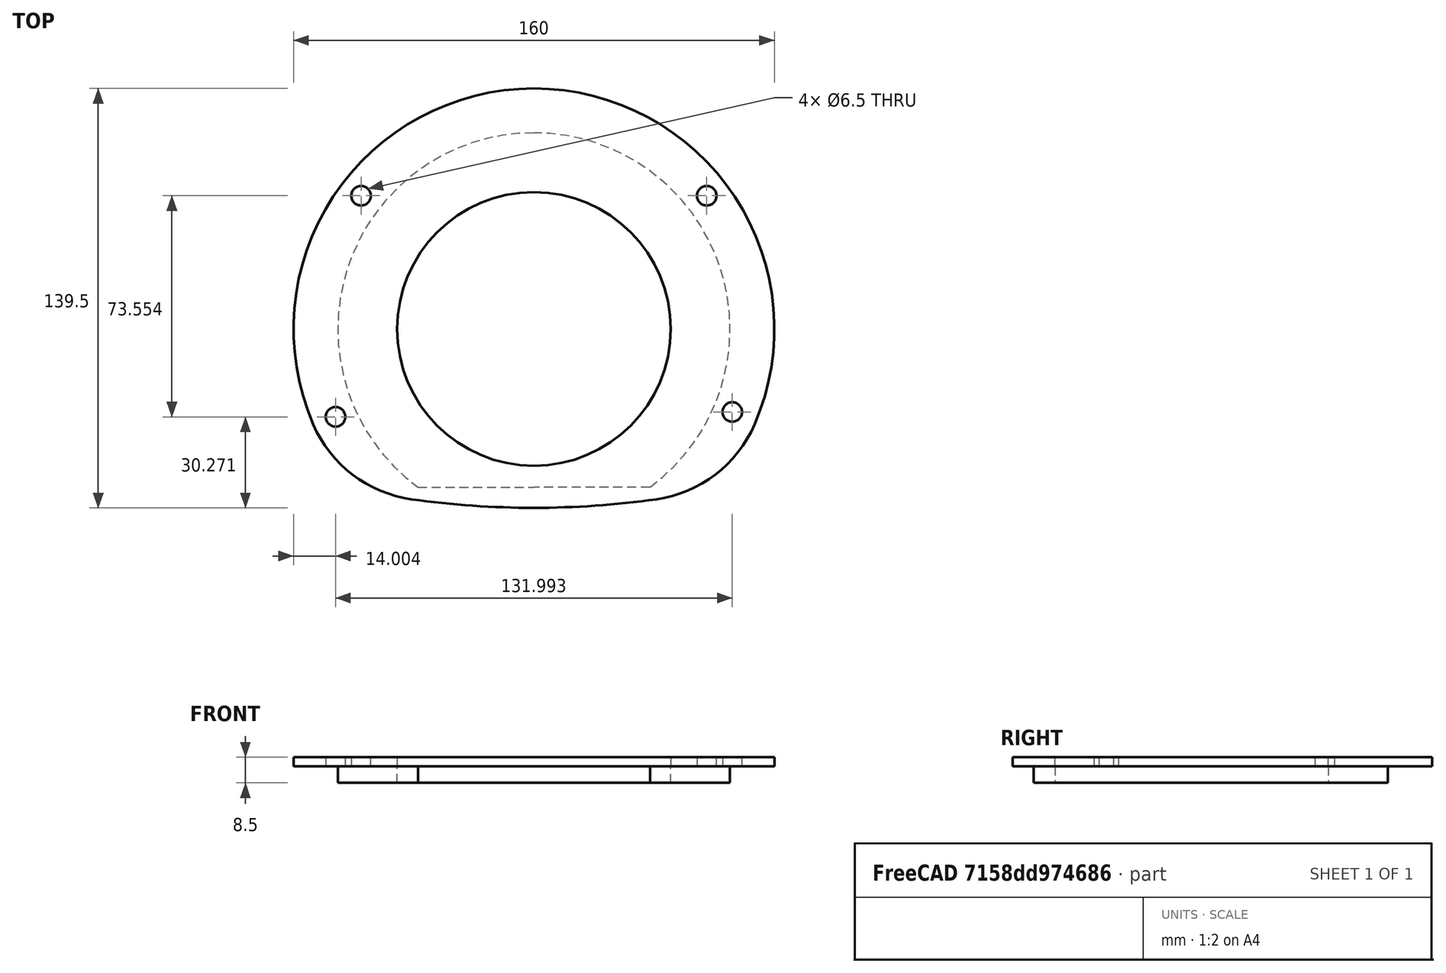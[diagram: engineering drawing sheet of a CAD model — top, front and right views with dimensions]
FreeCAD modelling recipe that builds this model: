
FCSTD DOCUMENT  (FreeCAD 0.20R29177 (Git))
Label: Отверстие Револьвера
License: All rights reserved
LicenseURL: http://en.wikipedia.org/wiki/All_rights_reserved
objects: Sketcher::SketchObject×3, PartDesign::Pad×2, Mesh::Feature×1, PartDesign::Mirrored×1, PartDesign::Pocket×1, PartDesign::Body×1
note: 11 computed .brp shape members not serialized (recipe doc carries the construction recipe); baked Part::Feature solids carry a one-line shape summary decoded from their .brp

FEATURE [Mesh::Feature] Hole1
FEATURE [Sketcher::SketchObject] Sketch
  FullyConstrained = true
  MapMode = 5
  Support = -> [XY_Plane]
  sketch-geometry (8):
    g0: ArcOfCircle CenterX=0 CenterY=0 CenterZ=0 NormalX=0 NormalY=0 NormalZ=1 AngleXU=0 Radius=80 StartAngle=5.87558 EndAngle=7.85398
    g1: ArcOfCircle CenterX=0 CenterY=233.5 CenterZ=0 NormalX=0 NormalY=0 NormalZ=1 AngleXU=0 Radius=293 StartAngle=4.71239 EndAngle=4.85183
    g2: LineSegment StartX=-5.38e-14 StartY=-59.5 StartZ=0 EndX=-8.4e-15 EndY=-45.5 EndZ=0
    g3: ArcOfCircle CenterX=0 CenterY=0 CenterZ=0 NormalX=0 NormalY=0 NormalZ=1 AngleXU=0 Radius=45.5 StartAngle=4.71239 EndAngle=7.85398
    g4: LineSegment StartX=1.39e-14 StartY=45.5 StartZ=0 EndX=2.45e-14 EndY=80 EndZ=0
    g5: ArcOfCircle CenterX=34.8867 CenterY=-15.0637 CenterZ=0 NormalX=0 NormalY=0 NormalZ=1 AngleXU=0 Radius=42 StartAngle=4.85183 EndAngle=5.87558
    g6: ArcOfCircle CenterX=0 CenterY=0 CenterZ=0 NormalX=0 NormalY=0 NormalZ=1 AngleXU=0 Radius=65.25 StartAngle=5.3456 EndAngle=7.85398
    g7: LineSegment StartX=38.6109 StartY=-52.6 StartZ=0 EndX=0 EndY=-52.6 EndZ=0
  constraints (27):
    c: Coincident(g0,g-1)
    c: PointOnObject(g0,g-2)
    c: PointOnObject(g1,g-2)
    c: Diameter(g0) = 160
    c: PointOnObject(g1,g-2)
    c: Coincident(g2,g1)
    c: PointOnObject(g2,g-2)
    c: Coincident(g3,g0)
    c: PointOnObject(g3,g-2)
    c: Coincident(g3,g2)
    c: Coincident(g4,g3)
    c: Coincident(g4,g0)
    c: Diameter(g3) = 91
    c: Distance(g2) = 14
    c: Radius(g1) = 293
    c: Coincident(g5,g0)
    c: Coincident(g5,g1)
    c: Tangent(g1,g5)
    c: Tangent(g5,g0)
    c: Diameter(g5) = 84
    c: Coincident(g6,g0)
    c: PointOnObject(g6,g4)
    c: Coincident(g7,g6)
    c: PointOnObject(g7,g-2)
    c: Horizontal(g7)
    c: Diameter(g6) = 130.5
    c: Distance(g7,g-1) = 52.6
FEATURE [PartDesign::Pad] Pad
  Direction = (1,1,1)
  Length = 3
  Length2 = 100
  Profile = -> Sketch
  Type = 0
FEATURE [Sketcher::SketchObject] Sketch001
  FullyConstrained = true
  MapMode = 5
  Support = -> [XY_Plane]
  expr: Constraints[12] = Sketch.Constraints[12]
  expr: Constraints[13] = Sketch.Constraints[13]
  expr: Constraints[14] = Sketch.Constraints[14]
  expr: Constraints[19] = Sketch.Constraints[19]
  expr: Constraints[25] = Sketch.Constraints[25]
  expr: Constraints[26] = Sketch.Constraints[26]
  expr: Constraints[3] = Sketch.Constraints[3]
  sketch-geometry (10):
    g0: ArcOfCircle CenterX=0 CenterY=0 CenterZ=0 NormalX=0 NormalY=0 NormalZ=1 AngleXU=0 Radius=80 StartAngle=5.87558 EndAngle=7.85398
    g1: ArcOfCircle CenterX=0 CenterY=233.5 CenterZ=0 NormalX=0 NormalY=0 NormalZ=1 AngleXU=0 Radius=293 StartAngle=4.71239 EndAngle=4.85183
    g2: LineSegment StartX=0 StartY=-59.5 StartZ=0 EndX=0 EndY=-45.5 EndZ=0
    g3: ArcOfCircle CenterX=0 CenterY=0 CenterZ=0 NormalX=0 NormalY=0 NormalZ=1 AngleXU=0 Radius=45.5 StartAngle=4.71239 EndAngle=7.85398
    g4: LineSegment StartX=0 StartY=45.5 StartZ=0 EndX=0 EndY=80 EndZ=0
    g5: ArcOfCircle CenterX=34.8867 CenterY=-15.0637 CenterZ=0 NormalX=0 NormalY=0 NormalZ=1 AngleXU=0 Radius=42 StartAngle=4.85183 EndAngle=5.87558
    g6: ArcOfCircle CenterX=0 CenterY=0 CenterZ=0 NormalX=0 NormalY=0 NormalZ=1 AngleXU=0 Radius=65.25 StartAngle=5.3456 EndAngle=7.85398
    g7: LineSegment StartX=38.6109 StartY=-52.6 StartZ=0 EndX=0 EndY=-52.6 EndZ=0
    g8: LineSegment StartX=0 StartY=65.25 StartZ=0 EndX=0 EndY=45.5 EndZ=0
    g9: LineSegment StartX=0 StartY=-52.6 StartZ=0 EndX=0 EndY=-45.5 EndZ=0
  constraints (31):
    c: Coincident(g0,g-1)
    c: PointOnObject(g0,g-2)
    c: PointOnObject(g1,g-2)
    c: Diameter(g0) = 160
    c: PointOnObject(g1,g-2)
    c: Coincident(g2,g1)
    c: PointOnObject(g2,g-2)
    c: Coincident(g3,g0)
    c: PointOnObject(g3,g-2)
    c: Coincident(g3,g2)
    c: Coincident(g4,g3)
    c: Coincident(g4,g0)
    c: Diameter(g3) = 91
    c: Distance(g2) = 14
    c: Radius(g1) = 293
    c: Coincident(g5,g0)
    c: Coincident(g5,g1)
    c: Tangent(g1,g5)
    c: Tangent(g5,g0)
    c: Diameter(g5) = 84
    c: Coincident(g6,g0)
    c: PointOnObject(g6,g4)
    c: Coincident(g7,g6)
    c: PointOnObject(g7,g-2)
    c: Horizontal(g7)
    c: Diameter(g6) = 130.5
    c: Distance(g7,g-1) = 52.6
    c: Coincident(g8,g6)
    c: Coincident(g8,g3)
    c: Coincident(g9,g7)
    c: Coincident(g9,g3)
FEATURE [PartDesign::Pad] Pad001
  BaseFeature = -> Pad
  Direction = (1,1,1)
  Length = 5.5
  Length2 = 100
  Profile = -> Sketch001
  Reversed = true
  Type = 0
FEATURE [PartDesign::Mirrored] Mirrored
  BaseFeature = -> Pad001
  MirrorPlane = -> Sketch [V_Axis]
  Originals = -> [Pad,Pad001]
FEATURE [Sketcher::SketchObject] Sketch002
  FullyConstrained = false
  MapMode = 5
  Support = -> [XY_Plane]
  sketch-geometry (7):
    g0: Circle CenterX=-65.9957 CenterY=-30.2293 CenterZ=0 NormalX=0 NormalY=0 NormalZ=1 AngleXU=0 Radius=3.25
    g1: Circle CenterX=-57.5114 CenterY=44.325 CenterZ=0 NormalX=0 NormalY=0 NormalZ=1 AngleXU=0 Radius=3.25
    g2: Circle CenterX=57.505 CenterY=44.3156 CenterZ=0 NormalX=0 NormalY=0 NormalZ=1 AngleXU=0 Radius=3.25
    g3: Circle CenterX=65.9971 CenterY=-27.6219 CenterZ=0 NormalX=0 NormalY=0 NormalZ=1 AngleXU=0 Radius=3.25
    g4: LineSegment StartX=-57.5114 StartY=44.325 StartZ=0 EndX=0 EndY=44.325 EndZ=0
    g5: LineSegment StartX=57.505 StartY=44.3156 StartZ=0 EndX=0 EndY=44.3156 EndZ=0
    g6: Circle CenterX=-65.9957 CenterY=-29.2293 CenterZ=0 NormalX=0 NormalY=0 NormalZ=1 AngleXU=0 Radius=3.25
  constraints (15):
    c: Diameter(g1) = 6.5
    c: Equal(g0,g3)
    c: Equal(g3,g2)
    c: Equal(g2,g1)
    c: Coincident(g4,g1)
    c: PointOnObject(g4,g-2)
    c: Horizontal(g4)
    c: Coincident(g5,g2)
    c: PointOnObject(g5,g-2)
    c: Horizontal(g5)
    c: DistanceX(g0) = -65.9957
    c: DistanceY(g0) = -30.2293
    c: Equal(g6,g0)
    c: Vertical(g0,g6)
    c: DistanceY(g0,g6) = 1
FEATURE [PartDesign::Pocket] Pocket
  BaseFeature = -> Mirrored
  Direction = (1,1,1)
  Length = 5
  Length2 = 100
  Profile = -> Sketch002
  Reversed = true
  Type = 1
FEATURE [PartDesign::Body] Body
  Group = -> [Sketch,Pad,Sketch001,Pad001,Mirrored,Sketch002,Pocket]
  Origin = -> Origin
  Tip = -> Pocket
